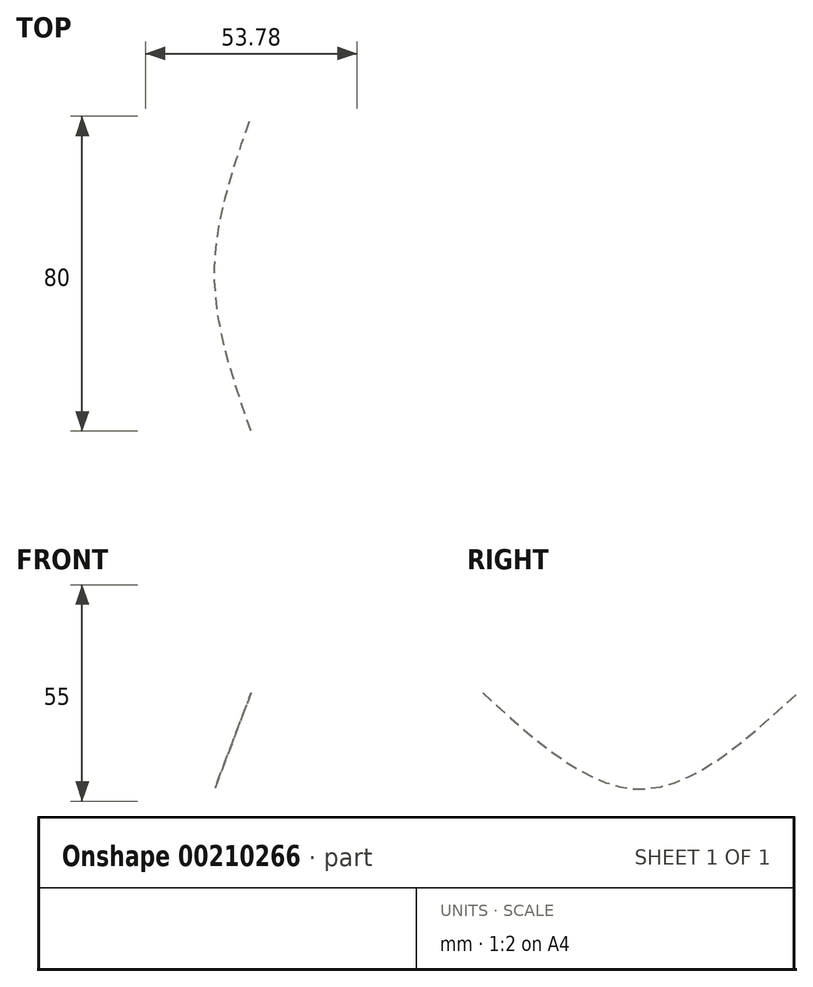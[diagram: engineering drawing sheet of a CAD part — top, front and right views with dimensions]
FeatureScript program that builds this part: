
annotation { "Feature Type Name" : "Feature", "Feature Type Description" : "" }
export const myFeature = defineFeature(function(context is Context, id is Id, definition is map)
    precondition{}
    {
        {
            var Q0;
            Q0=qCreatedBy(makeId("Front.planeOp"),FACE);
            var sketch = newSketch(context, id + "F0", { "sketchPlane" : qUnion([Q0])});
            skCircle(sketch, "E0", {"center": v(0, 0) * mm, "radius": 27.5 * mm});
            skCircle(sketch, "E1.cCircle", {"center": v(0, 0) * mm, "radius": 22.5 * mm, "construction": true});
            skLineSegment(sketch, "E1.0", {"start": v(-7.31, 22.5) * mm, "end": v(7.31, 22.5) * mm});
            skLineSegment(sketch, "E1.1", {"start": v(7.31, 22.5) * mm, "end": v(19.14, 13.9) * mm});
            skLineSegment(sketch, "E1.2", {"start": v(19.14, 13.9) * mm, "end": v(23.66, 0) * mm});
            skLineSegment(sketch, "E1.3", {"start": v(23.66, 0) * mm, "end": v(19.14, -13.9) * mm});
            skLineSegment(sketch, "E1.4", {"start": v(19.14, -13.9) * mm, "end": v(7.31, -22.5) * mm});
            skLineSegment(sketch, "E1.5", {"start": v(7.31, -22.5) * mm, "end": v(-7.31, -22.5) * mm});
            skLineSegment(sketch, "E1.6", {"start": v(-7.31, -22.5) * mm, "end": v(-19.14, -13.9) * mm});
            skLineSegment(sketch, "E1.7", {"start": v(-19.14, -13.9) * mm, "end": v(-23.66, 0) * mm});
            skLineSegment(sketch, "E1.8", {"start": v(-23.66, 0) * mm, "end": v(-19.14, 13.9) * mm});
            skLineSegment(sketch, "E1.9", {"start": v(-19.14, 13.9) * mm, "end": v(-7.31, 22.5) * mm});
            skPoint(sketch, "E1.0.midPoint", {"position": v(0, 22.5) * mm});
            skSolve(sketch);
        }
        {
            var Q0;
            Q0=qCreatedBy(makeId("Front.planeOp"),FACE);
            var sketch = newSketch(context, id + "F1", { "sketchPlane" : qUnion([Q0])});
            skLineSegment(sketch, "E2", {"start": v(0, 0) * mm, "end": v(0, 28.3) * mm, "construction": true});
            skArc(sketch, "E3", {"start": v(5.06, 26.62) * mm, "mid": v(2.57, 27.28) * mm, "end": v(0, 27.5) * mm});
            skArc(sketch, "E4", {"start": v(7.31, 22.5) * mm, "mid": v(6.97, 24.99) * mm, "end": v(5.06, 26.62) * mm});
            skLineSegment(sketch, "E5", {"start": v(0, 0) * mm, "end": v(8.5, 26.17) * mm, "construction": true});
            skLineSegment(sketch, "E6", {"start": v(7.31, 22.5) * mm, "end": v(8.2, 26.36) * mm, "construction": true});
            skArc(sketch, "E7.MirrorCS", {"start": v(-5.06, 26.62) * mm, "mid": v(-2.57, 27.28) * mm, "end": v(0, 27.5) * mm});
            skArc(sketch, "E8.MirrorCS", {"start": v(-7.31, 22.5) * mm, "mid": v(-6.97, 24.99) * mm, "end": v(-5.06, 26.62) * mm});
            skSolve(sketch);
        }
        {
            var Q0;
            Q0=qCreatedBy(makeId("Front.planeOp"),FACE);
            var sketch = newSketch(context, id + "F2", { "sketchPlane" : qUnion([Q0])});
            skArc(sketch, "E9.0", {"start": v(-6.85, 25.2) * mm, "mid": v(-6.07, 26.06) * mm, "end": v(-5.06, 26.62) * mm});
            skArc(sketch, "E10.0", {"start": v(-5.06, 26.62) * mm, "mid": v(-2.57, 27.28) * mm, "end": v(0, 27.5) * mm});
            skArc(sketch, "E11.0", {"start": v(5.06, 26.62) * mm, "mid": v(2.57, 27.28) * mm, "end": v(0, 27.5) * mm});
            skArc(sketch, "E12.0", {"start": v(6.85, 25.2) * mm, "mid": v(6.07, 26.06) * mm, "end": v(5.06, 26.62) * mm});
            skArc(sketch, "E13.1.0", {"start": v(-20.35, 16.36) * mm, "mid": v(-20.23, 17.5) * mm, "end": v(-19.74, 18.56) * mm});
            skArc(sketch, "E13.1.1", {"start": v(-19.74, 18.56) * mm, "mid": v(-18.11, 20.56) * mm, "end": v(-16.16, 22.25) * mm});
            skArc(sketch, "E13.1.2", {"start": v(-11.55, 24.51) * mm, "mid": v(-13.96, 23.58) * mm, "end": v(-16.16, 22.25) * mm});
            skArc(sketch, "E13.1.3", {"start": v(-9.27, 24.4) * mm, "mid": v(-10.4, 24.65) * mm, "end": v(-11.55, 24.51) * mm});
            skArc(sketch, "E13.2.0", {"start": v(-26.08, 1.27) * mm, "mid": v(-26.66, 2.28) * mm, "end": v(-26.88, 3.41) * mm});
            skArc(sketch, "E13.2.1", {"start": v(-26.88, 3.41) * mm, "mid": v(-26.74, 5.99) * mm, "end": v(-26.15, 8.5) * mm});
            skArc(sketch, "E13.2.2", {"start": v(-23.75, 13.04) * mm, "mid": v(-25.15, 10.87) * mm, "end": v(-26.15, 8.5) * mm});
            skArc(sketch, "E13.2.3", {"start": v(-21.84, 14.3) * mm, "mid": v(-22.9, 13.83) * mm, "end": v(-23.75, 13.04) * mm});
            skArc(sketch, "E13.3.0", {"start": v(-21.84, -14.3) * mm, "mid": v(-22.9, -13.83) * mm, "end": v(-23.75, -13.04) * mm});
            skArc(sketch, "E13.3.1", {"start": v(-23.75, -13.04) * mm, "mid": v(-25.15, -10.87) * mm, "end": v(-26.15, -8.5) * mm});
            skArc(sketch, "E13.3.2", {"start": v(-26.88, -3.41) * mm, "mid": v(-26.74, -5.99) * mm, "end": v(-26.15, -8.5) * mm});
            skArc(sketch, "E13.3.3", {"start": v(-26.08, -1.27) * mm, "mid": v(-26.66, -2.28) * mm, "end": v(-26.88, -3.41) * mm});
            skArc(sketch, "E13.4.0", {"start": v(-9.27, -24.4) * mm, "mid": v(-10.4, -24.65) * mm, "end": v(-11.55, -24.51) * mm});
            skArc(sketch, "E13.4.1", {"start": v(-11.55, -24.51) * mm, "mid": v(-13.96, -23.58) * mm, "end": v(-16.16, -22.25) * mm});
            skArc(sketch, "E13.4.2", {"start": v(-19.74, -18.56) * mm, "mid": v(-18.11, -20.56) * mm, "end": v(-16.16, -22.25) * mm});
            skArc(sketch, "E13.4.3", {"start": v(-20.35, -16.36) * mm, "mid": v(-20.23, -17.5) * mm, "end": v(-19.74, -18.56) * mm});
            skArc(sketch, "E13.5.0", {"start": v(6.85, -25.2) * mm, "mid": v(6.07, -26.06) * mm, "end": v(5.06, -26.62) * mm});
            skArc(sketch, "E13.5.1", {"start": v(5.06, -26.62) * mm, "mid": v(2.57, -27.28) * mm, "end": v(0, -27.5) * mm});
            skArc(sketch, "E13.5.2", {"start": v(-5.06, -26.62) * mm, "mid": v(-2.57, -27.28) * mm, "end": v(0, -27.5) * mm});
            skArc(sketch, "E13.5.3", {"start": v(-6.85, -25.2) * mm, "mid": v(-6.07, -26.06) * mm, "end": v(-5.06, -26.62) * mm});
            skArc(sketch, "E13.6.0", {"start": v(20.35, -16.36) * mm, "mid": v(20.23, -17.5) * mm, "end": v(19.74, -18.56) * mm});
            skArc(sketch, "E13.6.1", {"start": v(19.74, -18.56) * mm, "mid": v(18.11, -20.56) * mm, "end": v(16.16, -22.25) * mm});
            skArc(sketch, "E13.6.2", {"start": v(11.55, -24.51) * mm, "mid": v(13.96, -23.58) * mm, "end": v(16.16, -22.25) * mm});
            skArc(sketch, "E13.6.3", {"start": v(9.27, -24.4) * mm, "mid": v(10.4, -24.65) * mm, "end": v(11.55, -24.51) * mm});
            skArc(sketch, "E13.7.0", {"start": v(26.08, -1.27) * mm, "mid": v(26.66, -2.28) * mm, "end": v(26.88, -3.41) * mm});
            skArc(sketch, "E13.7.1", {"start": v(26.88, -3.41) * mm, "mid": v(26.74, -5.99) * mm, "end": v(26.15, -8.5) * mm});
            skArc(sketch, "E13.7.2", {"start": v(23.75, -13.04) * mm, "mid": v(25.15, -10.87) * mm, "end": v(26.15, -8.5) * mm});
            skArc(sketch, "E13.7.3", {"start": v(21.84, -14.3) * mm, "mid": v(22.9, -13.83) * mm, "end": v(23.75, -13.04) * mm});
            skArc(sketch, "E13.8.0", {"start": v(21.84, 14.3) * mm, "mid": v(22.9, 13.83) * mm, "end": v(23.75, 13.04) * mm});
            skArc(sketch, "E13.8.1", {"start": v(23.75, 13.04) * mm, "mid": v(25.15, 10.87) * mm, "end": v(26.15, 8.5) * mm});
            skArc(sketch, "E13.8.2", {"start": v(26.88, 3.41) * mm, "mid": v(26.74, 5.99) * mm, "end": v(26.15, 8.5) * mm});
            skArc(sketch, "E13.8.3", {"start": v(26.08, 1.27) * mm, "mid": v(26.66, 2.28) * mm, "end": v(26.88, 3.41) * mm});
            skArc(sketch, "E13.9.0", {"start": v(9.27, 24.4) * mm, "mid": v(10.4, 24.65) * mm, "end": v(11.55, 24.51) * mm});
            skArc(sketch, "E13.9.1", {"start": v(11.55, 24.51) * mm, "mid": v(13.96, 23.58) * mm, "end": v(16.16, 22.25) * mm});
            skArc(sketch, "E13.9.2", {"start": v(19.74, 18.56) * mm, "mid": v(18.11, 20.56) * mm, "end": v(16.16, 22.25) * mm});
            skArc(sketch, "E13.9.3", {"start": v(20.35, 16.36) * mm, "mid": v(20.23, 17.5) * mm, "end": v(19.74, 18.56) * mm});
            skPoint(sketch, "E13.center", {"position": v(0, 0) * mm});
            skPoint(sketch, "E14.visualSharp", {"position": v(7.31, 22.5) * mm});
            skArc(sketch, "E14.filletArc", {"start": v(6.85, 25.2) * mm, "mid": v(7.92, 24.37) * mm, "end": v(9.27, 24.4) * mm});
            skPoint(sketch, "E15.visualSharp", {"position": v(19.14, 13.9) * mm});
            skArc(sketch, "E15.filletArc", {"start": v(20.35, 16.36) * mm, "mid": v(20.73, 15.06) * mm, "end": v(21.84, 14.3) * mm});
            skPoint(sketch, "E16.visualSharp", {"position": v(23.66, 0) * mm});
            skArc(sketch, "E16.filletArc", {"start": v(26.08, 1.27) * mm, "mid": v(25.62, 0) * mm, "end": v(26.08, -1.27) * mm});
            skPoint(sketch, "E17.visualSharp", {"position": v(19.14, -13.9) * mm});
            skArc(sketch, "E17.filletArc", {"start": v(21.84, -14.3) * mm, "mid": v(20.73, -15.06) * mm, "end": v(20.35, -16.36) * mm});
            skPoint(sketch, "E18.visualSharp", {"position": v(7.31, -22.5) * mm});
            skArc(sketch, "E18.filletArc", {"start": v(9.27, -24.4) * mm, "mid": v(7.92, -24.37) * mm, "end": v(6.85, -25.2) * mm});
            skPoint(sketch, "E19.visualSharp", {"position": v(-7.31, -22.5) * mm});
            skArc(sketch, "E19.filletArc", {"start": v(-6.85, -25.2) * mm, "mid": v(-7.92, -24.37) * mm, "end": v(-9.27, -24.4) * mm});
            skPoint(sketch, "E20.visualSharp", {"position": v(-19.14, -13.9) * mm});
            skArc(sketch, "E20.filletArc", {"start": v(-20.35, -16.36) * mm, "mid": v(-20.73, -15.06) * mm, "end": v(-21.84, -14.3) * mm});
            skPoint(sketch, "E21.visualSharp", {"position": v(-23.66, 0) * mm});
            skArc(sketch, "E21.filletArc", {"start": v(-26.08, -1.27) * mm, "mid": v(-25.62, 0) * mm, "end": v(-26.08, 1.27) * mm});
            skPoint(sketch, "E22.visualSharp", {"position": v(-19.14, 13.9) * mm});
            skArc(sketch, "E22.filletArc", {"start": v(-21.84, 14.3) * mm, "mid": v(-20.73, 15.06) * mm, "end": v(-20.35, 16.36) * mm});
            skPoint(sketch, "E23.visualSharp", {"position": v(-7.31, 22.5) * mm});
            skArc(sketch, "E23.filletArc", {"start": v(-9.27, 24.4) * mm, "mid": v(-7.92, 24.37) * mm, "end": v(-6.85, 25.2) * mm});
            skSolve(sketch);
        }
        {
            var Q0;
            Q0=qCreatedBy(makeId("Top.planeOp"),FACE);
            var sketch = newSketch(context, id + "F3", { "sketchPlane" : qUnion([Q0])});
            skLineSegment(sketch, "E24", {"start": v(0, 0) * mm, "end": v(-46.19, 0) * mm, "construction": true});
            skPoint(sketch, "E25", {"position": v(0, -40) * mm});
            skPoint(sketch, "E26.MirrorP", {"position": v(0, 40) * mm});
            skSolve(sketch);
        }
        {
            var Q0;
            Q0=sQuery(id+"F3.wireOp",VERTEX,"E25");
            var Q1;
            Q1 = qSketchRegion(id + "F2", true);
            var Q2;
            Q2=sQuery(id+"F3.wireOp",VERTEX,"E26.MirrorP");
            loft(context, id + "F4", {"sheetProfilesArray" : [{ "sheetProfileEntities" : qUnion([Q0]) }, { "sheetProfileEntities" : qUnion([Q1]) }, { "sheetProfileEntities" : qUnion([Q2]) }]});
        }
    });
